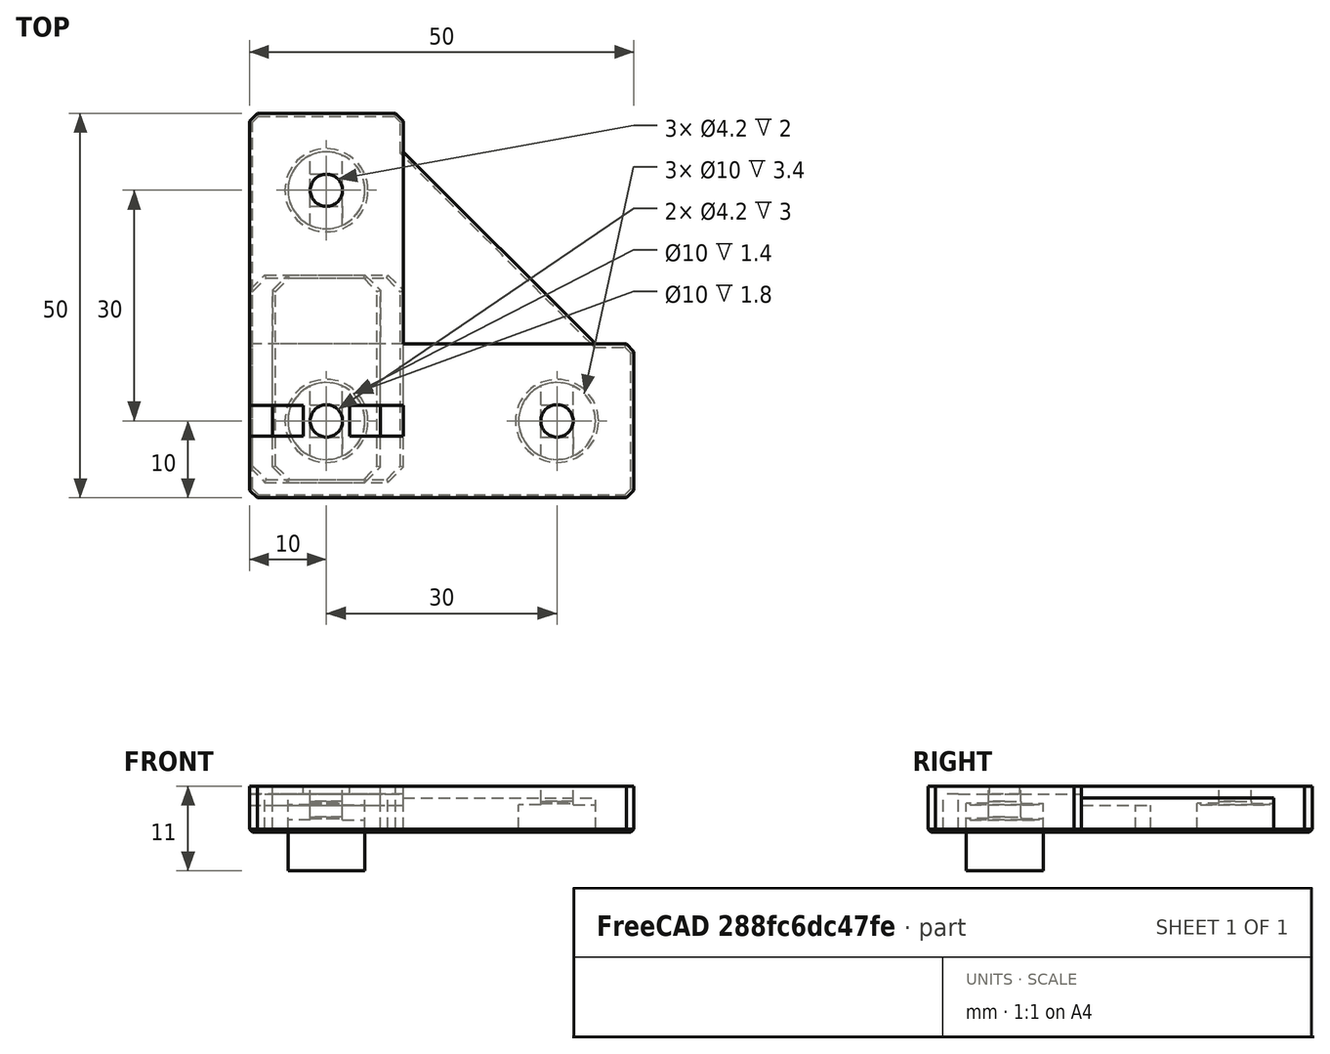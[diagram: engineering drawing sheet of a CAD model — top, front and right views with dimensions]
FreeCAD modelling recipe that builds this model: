
FCSTD DOCUMENT  (FreeCAD 0.18R14555 (Git shallow))
Label: filament-dryer-plate-fixer
License: All rights reserved
LicenseURL: http://en.wikipedia.org/wiki/All_rights_reserved
objects: Part::Box×14, Part::Cut×9, Part::Cylinder×6, Part::MultiFuse×6, Part::Chamfer×6, Part::Feature×6
note: 47 computed .brp shape members not serialized (recipe doc carries the construction recipe); baked Part::Feature solids carry a one-line shape summary decoded from their .brp

FEATURE [Part::Box] Box  label="Cube"
  AttacherType = Attacher::AttachEngine3D
  Height = 5
  Length = 14
  Placement = pos=(3,2,0) rot=(0,0,1;0rad)
  Width = 27
FEATURE [Part::Box] Box001  label="Cube001"
  AttacherType = Attacher::AttachEngine3D
  Height = 5
  Length = 20
  Placement = pos=(0,20,3.5) rot=(0,0,1;0rad)
  Width = 27
FEATURE [Part::Cylinder] Cylinder
  Angle = 360
  AttacherType = Attacher::AttachEngine3D
  Height = 7
  Placement = pos=(10,10,-5) rot=(0,0,1;0rad)
  Radius = 5
FEATURE [Part::Box] Box002  label="Cube002"
  AttacherType = Attacher::AttachEngine3D
  Height = 1
  Length = 4
  Placement = pos=(3,8,5) rot=(0,0,1;0rad)
  Width = 4
FEATURE [Part::Box] Box003  label="Cube003"
  AttacherType = Attacher::AttachEngine3D
  Height = 1
  Length = 4
  Placement = pos=(13,8,5) rot=(0,0,1;0rad)
  Width = 4
FEATURE [Part::Cut] Cut
  Base = -> Box
  Tool = -> Box001
FEATURE [Part::Cylinder] Cylinder001
  Angle = 360
  AttacherType = Attacher::AttachEngine3D
  Height = 10
  Placement = pos=(10,10,0) rot=(0,0,1;0rad)
  Radius = 2.1
FEATURE [Part::MultiFuse] Fusion
  Shapes = -> [Box003,Cut,Box002]
FEATURE [Part::Chamfer] Chamfer
  Base = -> Fusion
  Edges = 4 edges r=2: [Edge6,Edge8,Edge26,Edge30]
FEATURE [Part::Chamfer] Chamfer001
  Base = -> Chamfer
  Edges = 8 edges r=0.4: [Edge4,Edge21,Edge26,Edge27,Edge28,Edge29,Edge30,Edge31]
FEATURE [Part::Box] Box004  label="Cube004"
  AttacherType = Attacher::AttachEngine3D
  Height = 0.2
  Length = 10
  Placement = pos=(5,12.1,1.8) rot=(0,0,1;0rad)
  Width = 3
FEATURE [Part::Box] Box005  label="Cube005"
  AttacherType = Attacher::AttachEngine3D
  Height = 0.2
  Length = 10
  Placement = pos=(5,4.9,1.8) rot=(0,0,1;0rad)
  Width = 3
FEATURE [Part::Box] Box006  label="Cube006"
  AttacherType = Attacher::AttachEngine3D
  Height = 0.4
  Length = 3
  Placement = pos=(4.9,5,1.6) rot=(0,0,1;0rad)
  Width = 10
FEATURE [Part::Box] Box007  label="Cube007"
  AttacherType = Attacher::AttachEngine3D
  Height = 0.4
  Length = 3
  Placement = pos=(12.1,5,1.6) rot=(0,0,1;0rad)
  Width = 10
FEATURE [Part::MultiFuse] Fusion001
  Shapes = -> [Box004,Box007,Box005,Box006]
FEATURE [Part::Cut] Cut002
  Base = -> Chamfer001
  Tool = -> Cylinder001
FEATURE [Part::Box] Box008  label="Cube008"
  AttacherType = Attacher::AttachEngine3D
  Height = 6
  Length = 20
  Width = 50
FEATURE [Part::Box] Box009  label="Cube009"
  AttacherType = Attacher::AttachEngine3D
  Height = 6
  Length = 50
  Width = 20
FEATURE [Part::Feature] Body001
  Placement = pos=(20,20,0) rot=(0,0,1;0rad)
  shape: bbox 25 x 25 x 4.5 mm, 5 faces (baked)
FEATURE [Part::MultiFuse] Fusion002
  Shapes = -> [Body001,Box008,Box009]
FEATURE [Part::Cut] Cut003  label="screw-template"
  Base = -> Cylinder
  Tool = -> Fusion001
FEATURE [Part::Feature] Cut003001  label="screw-template001"
  shape: bbox 10 x 10 x 7 mm, 11 faces (baked)
FEATURE [Part::Cut] Cut003002  label="small"
  Base = -> Cut002
  Tool = -> Cut003001
FEATURE [Part::Feature] Cut003003  label="screw-template002"
  Placement = pos=(0,0,2) rot=(0,0,1;0rad)
  shape: bbox 10 x 10 x 7 mm, 11 faces (baked)
FEATURE [Part::Feature] Cut003004  label="screw-template003"
  Placement = pos=(0,30,2) rot=(0,0,1;0rad)
  shape: bbox 10 x 10 x 7 mm, 11 faces (baked)
FEATURE [Part::Feature] Cut003005  label="screw-template004"
  Placement = pos=(30,0,2) rot=(0,0,1;0rad)
  shape: bbox 10 x 10 x 7 mm, 11 faces (baked)
FEATURE [Part::Cylinder] Cylinder002
  Angle = 360
  AttacherType = Attacher::AttachEngine3D
  Height = 10
  Placement = pos=(10,10,0) rot=(0,0,1;0rad)
  Radius = 2.1
FEATURE [Part::Cylinder] Cylinder003
  Angle = 360
  AttacherType = Attacher::AttachEngine3D
  Height = 10
  Placement = pos=(40,10,0) rot=(0,0,1;0rad)
  Radius = 2.1
FEATURE [Part::Cylinder] Cylinder004
  Angle = 360
  AttacherType = Attacher::AttachEngine3D
  Height = 10
  Placement = pos=(10,40,0) rot=(0,0,1;0rad)
  Radius = 2.1
FEATURE [Part::MultiFuse] Fusion003
  Shapes = -> [Cylinder004,Cylinder002,Cylinder003]
FEATURE [Part::Cut] Cut003006
  Base = -> Fusion002
  Tool = -> Fusion003
FEATURE [Part::MultiFuse] Fusion004
  Shapes = -> [Cut003005,Cut003003,Cut003004]
FEATURE [Part::Cut] Cut003007
  Base = -> Cut003006
  Tool = -> Fusion004
FEATURE [Part::Chamfer] Chamfer002
  Base = -> Cut003007
  Edges = 5 edges r=1: [Edge1,Edge12,Edge18,Edge32,Edge50]
FEATURE [Part::Chamfer] Chamfer003  label="foot-plate"
  Base = -> Chamfer002
  Edges = 17 edges r=0.4: [Edge4,Edge10,Edge14,Edge16,Edge18,Edge36,Edge38,Edge40,Edge41,Edge42,Edge43,Edge44,Edge45,Edge47,Edge48,Edge49,Edge89]
FEATURE [Part::Box] Box010  label="Cube010"
  AttacherType = Attacher::AttachEngine3D
  Height = 5
  Length = 20
  Placement = pos=(0,2,0) rot=(0,0,1;0rad)
  Width = 27
FEATURE [Part::Box] Box011  label="Cube011"
  AttacherType = Attacher::AttachEngine3D
  Height = 5
  Length = 20
  Placement = pos=(0,20,3.5) rot=(0,0,1;0rad)
  Width = 27
FEATURE [Part::Cut] Cut003008
  Base = -> Box010
  Tool = -> Box011
FEATURE [Part::Cylinder] Cylinder005
  Angle = 360
  AttacherType = Attacher::AttachEngine3D
  Height = 10
  Placement = pos=(10,10,0) rot=(0,0,1;0rad)
  Radius = 2.1
FEATURE [Part::Feature] Cut003009  label="screw-template005"
  shape: bbox 10 x 10 x 7 mm, 11 faces (baked)
FEATURE [Part::Cut] Cut003010
  Base = -> Cut003008
  Tool = -> Cut003009
FEATURE [Part::Cut] Cut003011
  Base = -> Cut003010
  Tool = -> Cylinder005
FEATURE [Part::Box] Box012  label="Cube012"
  AttacherType = Attacher::AttachEngine3D
  Height = 1
  Length = 7
  Placement = pos=(0,8,5) rot=(0,0,1;0rad)
  Width = 4
FEATURE [Part::Box] Box013  label="Cube013"
  AttacherType = Attacher::AttachEngine3D
  Height = 1
  Length = 7
  Placement = pos=(13,8,5) rot=(0,0,1;0rad)
  Width = 4
FEATURE [Part::Chamfer] Chamfer004
  Base = -> Cut003011
  Edges = 4 edges r=2: [Edge4,Edge6,Edge15,Edge20]
FEATURE [Part::MultiFuse] Fusion005
  Shapes = -> [Chamfer004,Box012,Box013]
FEATURE [Part::Chamfer] Chamfer005  label="big"
  Base = -> Fusion005
  Edges = 9 edges r=0.4: [Edge6,Edge25,Edge29,Edge30,Edge31,Edge32,Edge33,Edge34,Edge35]
